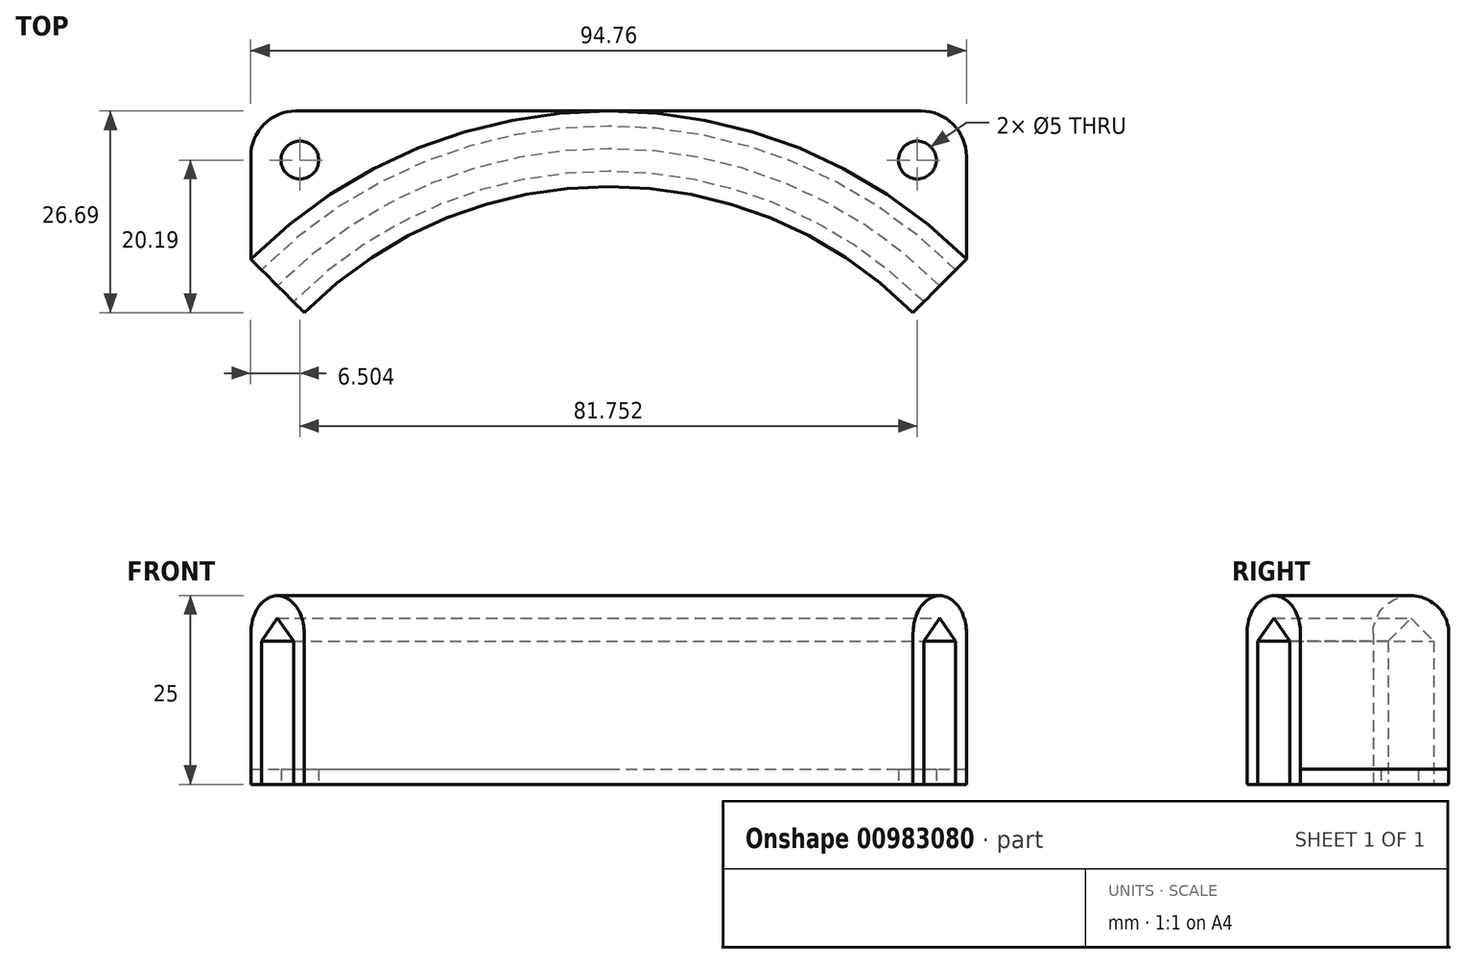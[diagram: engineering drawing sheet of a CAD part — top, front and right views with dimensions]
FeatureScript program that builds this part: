
annotation { "Feature Type Name" : "Feature", "Feature Type Description" : "" }
export const myFeature = defineFeature(function(context is Context, id is Id, definition is map)
    precondition{}
    {
        {
            var Q0;
            Q0=qCreatedBy(makeId("Right.planeOp"),FACE);
            var sketch = newSketch(context, id + "F0", { "sketchPlane" : qUnion([Q0])});
            skLineSegment(sketch, "E0", {"start": v(65, 0) * mm, "end": v(65, 19) * mm});
            skLineSegment(sketch, "E1", {"start": v(65, 19) * mm, "end": v(62, 22) * mm});
            skLineSegment(sketch, "E2", {"start": v(62, 22) * mm, "end": v(59, 19) * mm});
            skLineSegment(sketch, "E3", {"start": v(59, 19) * mm, "end": v(59, 0) * mm});
            skLineSegment(sketch, "E4", {"start": v(59, 0) * mm, "end": v(57, 0) * mm});
            skLineSegment(sketch, "E5", {"start": v(57, 0) * mm, "end": v(57, 20) * mm});
            skLineSegment(sketch, "E6", {"start": v(65, 0) * mm, "end": v(67, 0) * mm});
            skLineSegment(sketch, "E7", {"start": v(67, 0) * mm, "end": v(67, 20) * mm});
            skArc(sketch, "E8", {"start": v(67, 20) * mm, "mid": v(62, 25) * mm, "end": v(57, 20) * mm});
            skLineSegment(sketch, "E9", {"start": v(0, 0) * mm, "end": v(0, 22) * mm});
            skSolve(sketch);
        }
        {
            var Q0;
            Q0=makeQuery(id+"F0.imprint","IMPRINT",FACE,{"disambiguationData":[TD([[makeQuery(id+"F0.imprint","IMPRINT",EDGE,{"derivedFrom":sQuery(id+"F0.wireOp",EDGE,"E0")}),-1.0]])]});
            var Q1;
            Q1=sQuery(id+"F0.wireOp",EDGE,"E9");
            revolve(context, id + "F1", {"surfaceOperationType" : NewSurfaceOperationType.NEW, "entities" : qUnion([Q0]), "axis" : qUnion([Q1]), "revolveType" : RevolveType.SYMMETRIC, "angle" : 90 * degree});
        }
        {
            var Q0;
            Q0=makeQuery(id+"F1.opRevolve","SWEPT_FACE",FACE,{"disambiguationData":[OSD([sQuery(id+"F0.wireOp",EDGE,"E6")])]});
            var sketch = newSketch(context, id + "F2", { "sketchPlane" : qUnion([Q0])});
            skLineSegment(sketch, "E10", {"start": v(-47.38, -47.38) * mm, "end": v(-47.38, -67) * mm});
            skPoint(sketch, "E10.endSnap0", {"position": v(0, -67) * mm});
            skLineSegment(sketch, "E11", {"start": v(-47.38, -67) * mm, "end": v(47.38, -67) * mm});
            skLineSegment(sketch, "E12", {"start": v(47.38, -67) * mm, "end": v(47.38, -47.38) * mm});
            skCircle(sketch, "E13", {"center": v(-40.88, -60.5) * mm, "radius": 2.5 * mm});
            skCircle(sketch, "E14.MirrorC", {"center": v(40.88, -60.5) * mm, "radius": 2.5 * mm});
            skSolve(sketch);
        }
        {
            var Q0;
            {var subQ0=sQuery(id+"F2.wireOp",EDGE,"E10");Q0=makeQuery(id+"F2.imprint","IMPRINT",FACE,{"disambiguationData":[TD([[makeQuery(id+"F2.imprint","IMPRINT",EDGE,{"derivedFrom":subQ0}),1.0]])]});}
            var Q1;
            {var subQ0=sQuery(id+"F2.wireOp",EDGE,"E12");Q1=makeQuery(id+"F2.imprint","IMPRINT",FACE,{"disambiguationData":[TD([[makeQuery(id+"F2.imprint","IMPRINT",EDGE,{"derivedFrom":subQ0}),1.0]])]});}
            extrude(context, id + "F3", {"entities" : qUnion([Q0, Q1]), "operationType" : NewBodyOperationType.ADD, "oppositeDirection" : true, "depth" : 2 * mm, "offsetDistance" : 25 * mm});
        }
        {
            var Q0;
            Q0=makeQuery(id+"F3.opExtrude","SWEPT_EDGE",EDGE,{"disambiguationData":[OSD([sQuery(id+"F2.wireOp",EDGE,"E10"),sQuery(id+"F2.wireOp",EDGE,"E11")])]});
            var Q1;
            Q1=makeQuery(id+"F3.opExtrude","SWEPT_EDGE",EDGE,{"disambiguationData":[OSD([sQuery(id+"F2.wireOp",EDGE,"E11"),sQuery(id+"F2.wireOp",EDGE,"E12")])]});
            fillet(context, id + "F4", {"entities" : qUnion([Q0, Q1]), "radius" : 6 * mm, "tangentPropagation" : true, "allowEdgeOverflow" : false});
        }
    });
